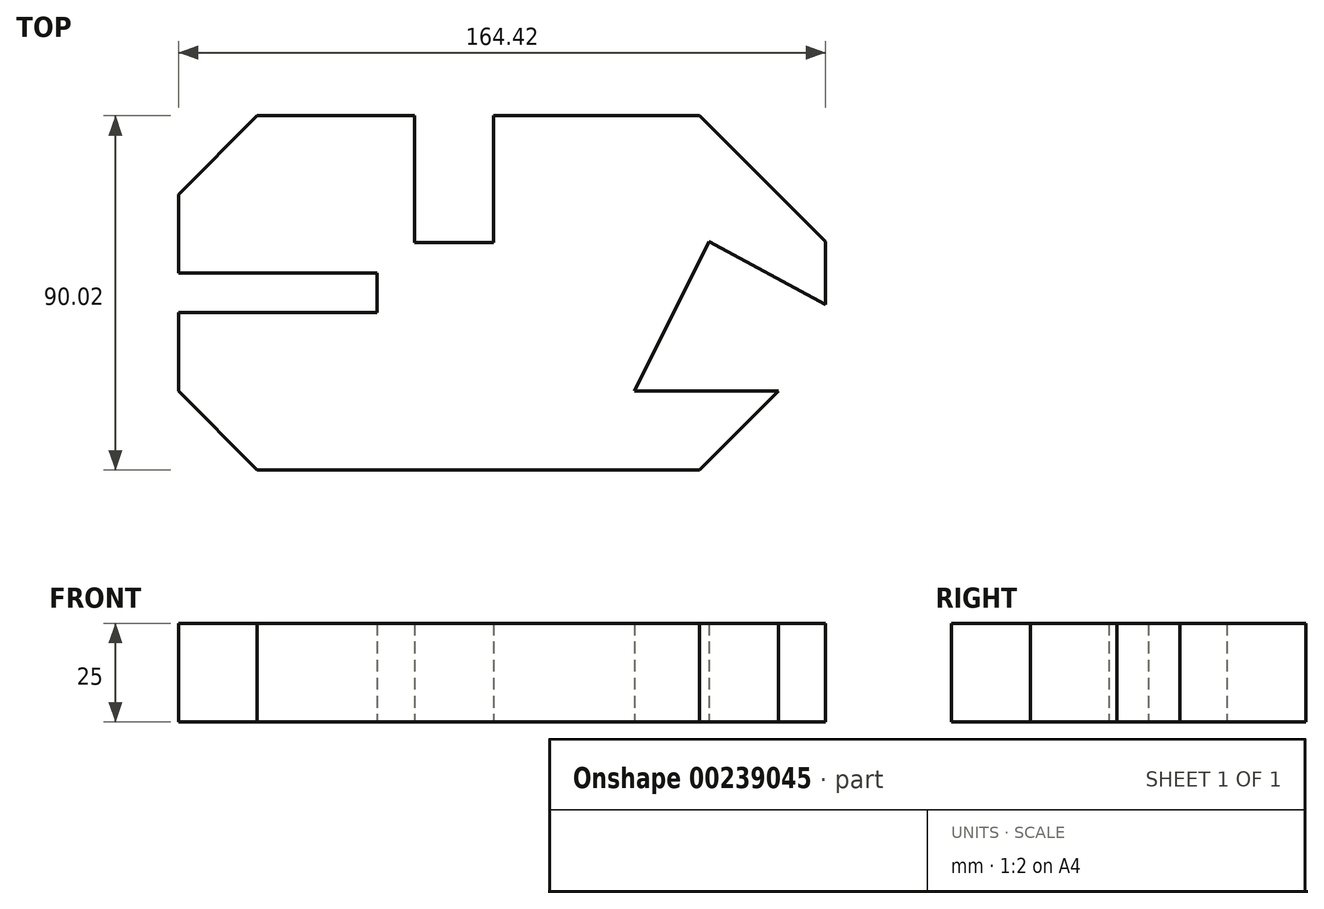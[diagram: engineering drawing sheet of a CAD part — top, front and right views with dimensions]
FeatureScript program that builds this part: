
annotation { "Feature Type Name" : "Feature", "Feature Type Description" : "" }
export const myFeature = defineFeature(function(context is Context, id is Id, definition is map)
    precondition{}
    {
        {
            var Q0;
            Q0=qCreatedBy(makeId("Top.planeOp"),FACE);
            var sketch = newSketch(context, id + "F0", { "sketchPlane" : qUnion([Q0])});
            skLineSegment(sketch, "E0", {"start": v(-88.4, -29.36) * mm, "end": v(24, -29.36) * mm});
            skLineSegment(sketch, "E1", {"start": v(-88.4, -29.36) * mm, "end": v(-108.41, -9.35) * mm});
            skLineSegment(sketch, "E2", {"start": v(24, -29.36) * mm, "end": v(44, -9.35) * mm});
            skLineSegment(sketch, "E3", {"start": v(-108.41, -9.35) * mm, "end": v(-108.41, 10.65) * mm});
            skLineSegment(sketch, "E4", {"start": v(-108.41, 10.65) * mm, "end": v(-57.91, 10.65) * mm});
            skLineSegment(sketch, "E5", {"start": v(-57.91, 10.65) * mm, "end": v(-57.91, 20.65) * mm});
            skLineSegment(sketch, "E6", {"start": v(-57.91, 20.65) * mm, "end": v(-108.41, 20.65) * mm});
            skLineSegment(sketch, "E7", {"start": v(-108.41, 20.65) * mm, "end": v(-108.41, 40.65) * mm});
            skLineSegment(sketch, "E8", {"start": v(-108.41, 40.65) * mm, "end": v(-88.4, 60.66) * mm});
            skLineSegment(sketch, "E9", {"start": v(-88.4, 60.66) * mm, "end": v(-48.4, 60.66) * mm});
            skLineSegment(sketch, "E10", {"start": v(-48.4, 60.66) * mm, "end": v(-48.4, 28.36) * mm});
            skLineSegment(sketch, "E11", {"start": v(-48.4, 28.36) * mm, "end": v(-28.4, 28.36) * mm});
            skLineSegment(sketch, "E12", {"start": v(-28.4, 28.36) * mm, "end": v(-28.4, 60.66) * mm});
            skLineSegment(sketch, "E13", {"start": v(-28.4, 60.66) * mm, "end": v(24, 60.66) * mm});
            skLineSegment(sketch, "E14", {"start": v(24, 60.66) * mm, "end": v(57.32, 60.66) * mm, "construction": true});
            skLineSegment(sketch, "E15", {"start": v(24, 60.66) * mm, "end": v(56, 28.65) * mm});
            skLineSegment(sketch, "E16", {"start": v(56, 28.65) * mm, "end": v(56, 12.65) * mm});
            skLineSegment(sketch, "E17", {"start": v(56, 12.65) * mm, "end": v(26.35, 28.65) * mm});
            skLineSegment(sketch, "E18", {"start": v(44, -9.35) * mm, "end": v(7.53, -9.35) * mm});
            skLineSegment(sketch, "E19", {"start": v(26.35, 28.65) * mm, "end": v(7.53, -9.35) * mm});
            skSolve(sketch);
        }
        {
            var Q0;
            Q0=makeQuery(id+"F0.imprint","IMPRINT",FACE,{"disambiguationData":[TD([[makeQuery(id+"F0.imprint","IMPRINT",EDGE,{"derivedFrom":sQuery(id+"F0.wireOp",EDGE,"E0")}),1.0]])]});
            extrude(context, id + "F1", {"entities" : qUnion([Q0]), "depth" : 25 * mm});
        }
    });
